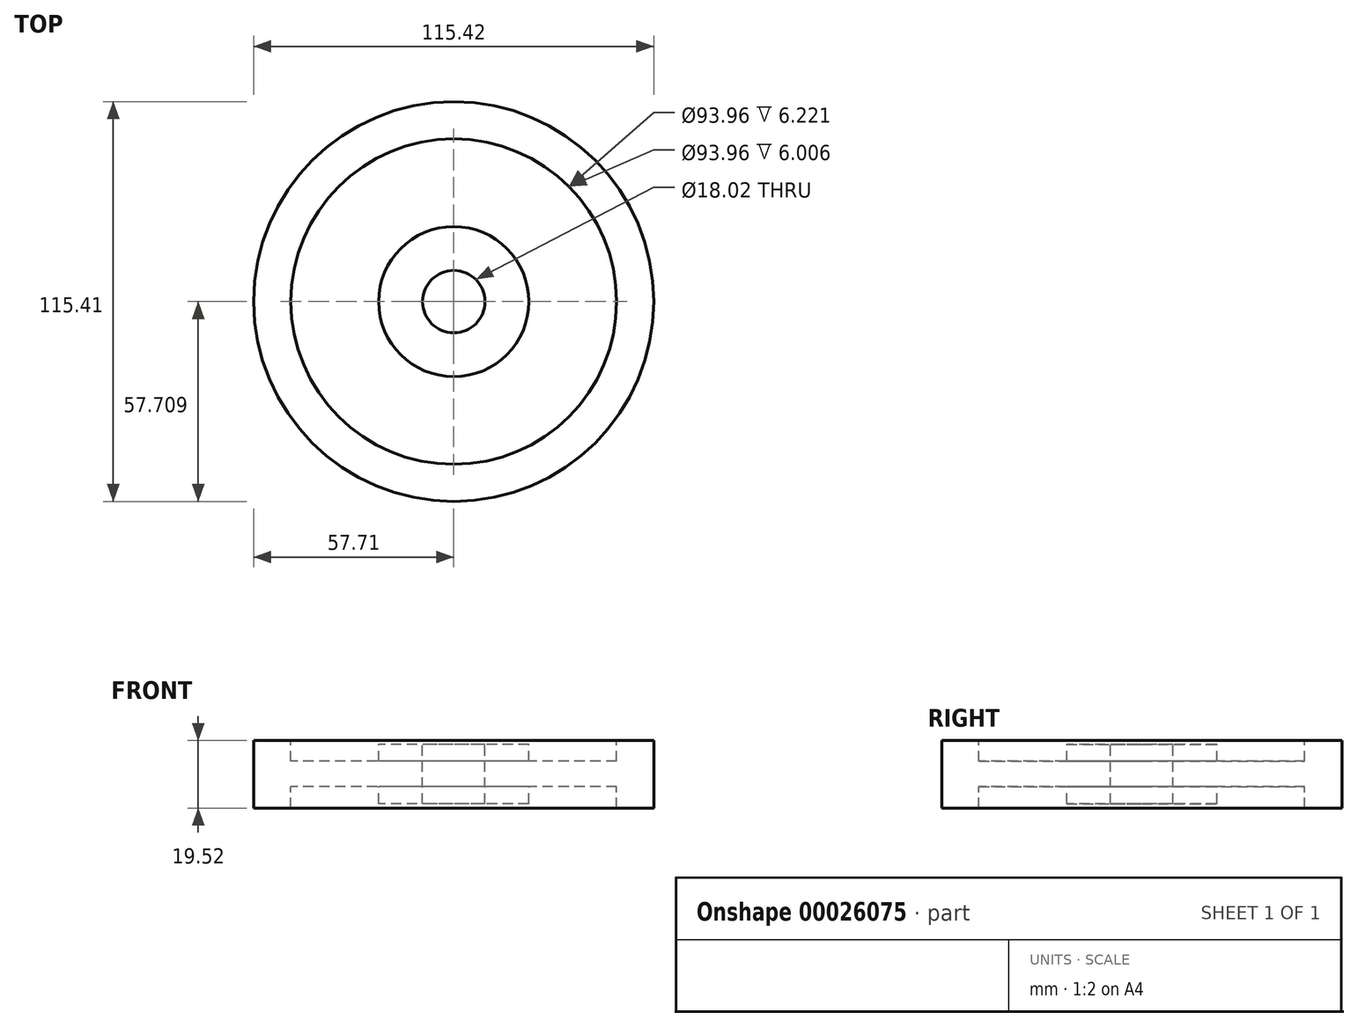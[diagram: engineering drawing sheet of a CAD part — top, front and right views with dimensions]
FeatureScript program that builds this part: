
annotation { "Feature Type Name" : "Feature", "Feature Type Description" : "" }
export const myFeature = defineFeature(function(context is Context, id is Id, definition is map)
    precondition{}
    {
        {
            var Q0;
            Q0=qCreatedBy(makeId("Right.planeOp"),FACE);
            var sketch = newSketch(context, id + "F0", { "sketchPlane" : qUnion([Q0])});
            skLineSegment(sketch, "E0.bottom", {"start": v(-45.57, 23.2) * mm, "end": v(-32.91, 23.2) * mm});
            skLineSegment(sketch, "E0.top", {"start": v(-45.57, 6.04) * mm, "end": v(-32.91, 6.04) * mm});
            skLineSegment(sketch, "E0.left", {"start": v(-45.57, 23.2) * mm, "end": v(-45.57, 6.04) * mm});
            skLineSegment(sketch, "E0.right", {"start": v(-32.91, 23.2) * mm, "end": v(-32.91, 6.04) * mm});
            skLineSegment(sketch, "E1.bottom", {"start": v(-32.91, 18.27) * mm, "end": v(-7.6, 18.27) * mm});
            skLineSegment(sketch, "E1.top", {"start": v(-32.91, 10.98) * mm, "end": v(-7.6, 10.98) * mm});
            skLineSegment(sketch, "E1.left", {"start": v(-32.91, 18.27) * mm, "end": v(-32.91, 10.98) * mm});
            skLineSegment(sketch, "E1.right", {"start": v(-7.6, 18.27) * mm, "end": v(-7.6, 10.98) * mm});
            skLineSegment(sketch, "E2.bottom", {"start": v(-7.6, 24.28) * mm, "end": v(3.12, 24.28) * mm});
            skLineSegment(sketch, "E2.top", {"start": v(-7.6, 4.76) * mm, "end": v(3.12, 4.76) * mm});
            skLineSegment(sketch, "E2.left", {"start": v(-7.6, 24.28) * mm, "end": v(-7.6, 4.76) * mm});
            skLineSegment(sketch, "E2.right", {"start": v(3.12, 24.28) * mm, "end": v(3.12, 4.76) * mm});
            skLineSegment(sketch, "E3", {"start": v(-54.58, 31.14) * mm, "end": v(-54.58, -11.76) * mm, "construction": true});
            skSolve(sketch);
        }
        {
            var Q0;
            Q0 = qSketchRegion(id + "F0", true);
            var Q1;
            Q1=sQuery(id+"F0.wireOp",EDGE,"E3");
            revolve(context, id + "F1", {"entities" : qUnion([Q0]), "axis" : qUnion([Q1]), "revolveType" : RevolveType.FULL});
        }
    });
